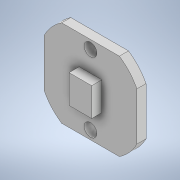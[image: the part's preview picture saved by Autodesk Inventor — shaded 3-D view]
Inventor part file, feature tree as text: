
AUTODESK INVENTOR PART (.ipt)
format: ipt  version: 2022 (Build 260153070, 153G)  size: 129,536 bytes
history: native  units: mm
features: sketch x3, extrude x2
ambient origin geometry x8: Origin, YZ Plane, XZ Plane, XY Plane, X Axis, Y Axis, Z Axis, Center Point
bodies: Solid1 (feature_tree)
feature tree (5):
  extrude  "Extrusion1"  Depth=16.0mm
  extrude  "Extrusion2"  Depth=8.0mm
  sketch  "Sketch3"  dims[d8=18.0mm d9=6.0mm d10=2.2mm d11=2.2mm d12=6.0mm d13=1.57mm d14=0.0mm d15=4.9mm d16=3.9mm d17=1.95mm d18=2.45mm d19=1.75mm d20=0.0mm d21=2.828427mm]
  sketch  "Sketch1"  dims[d3=15.0mm d4=16.0mm]
  sketch  "Sketch2"  dims[d6=7.5mm d7=8.0mm]
